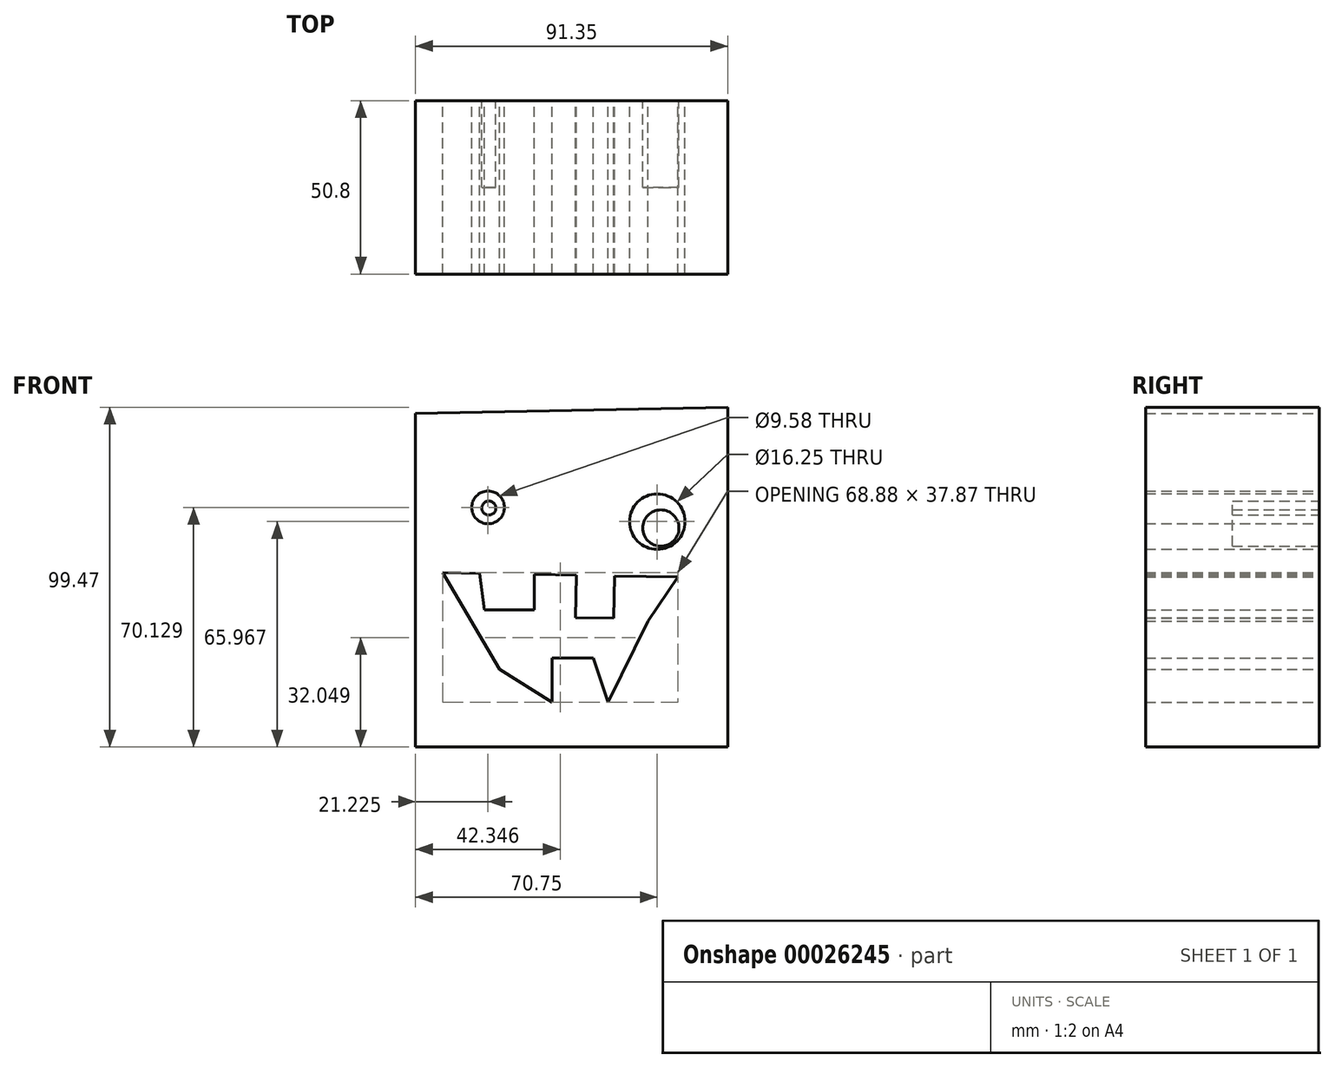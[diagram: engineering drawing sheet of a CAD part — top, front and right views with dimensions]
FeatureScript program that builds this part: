
annotation { "Feature Type Name" : "Feature", "Feature Type Description" : "" }
export const myFeature = defineFeature(function(context is Context, id is Id, definition is map)
    precondition{}
    {
        {
            var Q0;
            Q0=qCreatedBy(makeId("Front.planeOp"),FACE);
            var sketch = newSketch(context, id + "F0", { "sketchPlane" : qUnion([Q0])});
            skLineSegment(sketch, "E0", {"start": v(-46.82, 44.43) * mm, "end": v(-46.82, -53.17) * mm});
            skLineSegment(sketch, "E1", {"start": v(-46.82, -53.17) * mm, "end": v(44.53, -53.17) * mm});
            skLineSegment(sketch, "E2", {"start": v(44.53, -53.17) * mm, "end": v(44.53, 46.3) * mm});
            skLineSegment(sketch, "E3", {"start": v(44.53, 46.3) * mm, "end": v(-46.82, 44.43) * mm});
            skLineSegment(sketch, "E4.bottom", {"start": v(-30.59, 23.83) * mm, "end": v(-15.81, 23.83) * mm});
            skLineSegment(sketch, "E4.top", {"start": v(-30.59, 11.76) * mm, "end": v(-15.81, 11.76) * mm});
            skLineSegment(sketch, "E4.left", {"start": v(-30.59, 23.83) * mm, "end": v(-30.59, 11.76) * mm});
            skLineSegment(sketch, "E4.right", {"start": v(-15.81, 23.83) * mm, "end": v(-15.81, 11.76) * mm});
            skLineSegment(sketch, "E5.bottom", {"start": v(-11.44, 35.69) * mm, "end": v(33.71, 35.69) * mm});
            skLineSegment(sketch, "E5.top", {"start": v(-11.44, 4.47) * mm, "end": v(33.71, 4.47) * mm});
            skLineSegment(sketch, "E5.left", {"start": v(-11.44, 35.69) * mm, "end": v(-11.44, 4.47) * mm});
            skLineSegment(sketch, "E5.right", {"start": v(33.71, 35.69) * mm, "end": v(33.71, 4.47) * mm});
            skLineSegment(sketch, "E6", {"start": v(-38.91, -2.18) * mm, "end": v(-22.27, -30.48) * mm});
            skLineSegment(sketch, "E7", {"start": v(-22.27, -30.48) * mm, "end": v(-6.87, -40.06) * mm});
            skLineSegment(sketch, "E8", {"start": v(-6.87, -40.06) * mm, "end": v(9.57, -40.06) * mm});
            skLineSegment(sketch, "E9", {"start": v(9.57, -40.06) * mm, "end": v(21.23, -16.33) * mm});
            skLineSegment(sketch, "E10", {"start": v(21.23, -16.33) * mm, "end": v(29.96, -3.43) * mm});
            skLineSegment(sketch, "E11", {"start": v(29.96, -3.43) * mm, "end": v(-38.91, -2.18) * mm});
            skLineSegment(sketch, "E12", {"start": v(-28.1, -2.38) * mm, "end": v(-26.64, -13) * mm});
            skLineSegment(sketch, "E13", {"start": v(-26.64, -13) * mm, "end": v(-12.07, -13) * mm});
            skLineSegment(sketch, "E14", {"start": v(-12.07, -13) * mm, "end": v(-12.07, -2.67) * mm});
            skLineSegment(sketch, "E15", {"start": v(-12.07, -2.67) * mm, "end": v(11.44, -3.1) * mm});
            skLineSegment(sketch, "E16", {"start": v(11.44, -3.1) * mm, "end": v(11.21, -15.52) * mm});
            skLineSegment(sketch, "E17", {"start": v(11.21, -15.52) * mm, "end": v(0, -15.31) * mm});
            skLineSegment(sketch, "E18", {"start": v(0, -15.31) * mm, "end": v(0.23, -2.9) * mm});
            skLineSegment(sketch, "E19", {"start": v(-6.87, -40.06) * mm, "end": v(-6.87, -27.16) * mm});
            skLineSegment(sketch, "E20", {"start": v(-6.87, -27.16) * mm, "end": v(5.2, -27.16) * mm});
            skLineSegment(sketch, "E21", {"start": v(5.2, -27.16) * mm, "end": v(9.57, -40.06) * mm});
            skCircle(sketch, "E22", {"center": v(23.93, 12.8) * mm, "radius": 8.13 * mm});
            skCircle(sketch, "E23", {"center": v(-25.6, 16.96) * mm, "radius": 4.8 * mm});
            skSolve(sketch);
        }
        {
            var Q0;
            Q0=makeQuery(id+"F0.imprint","IMPRINT",FACE,{"disambiguationData":[TD([[makeQuery(id+"F0.imprint","IMPRINT",EDGE,{"derivedFrom":sQuery(id+"F0.wireOp",EDGE,"E0")}),1.0]])]});
            var Q1;
            Q1=makeQuery(id+"F0.imprint","IMPRINT",FACE,{"disambiguationData":[TD([[makeQuery(id+"F0.imprint","IMPRINT",EDGE,{"derivedFrom":sQuery(id+"F0.wireOp",EDGE,"E5.bottom")}),-1.0]])]});
            var Q2;
            Q2=makeQuery(id+"F0.imprint","IMPRINT",FACE,{"disambiguationData":[TD([[makeQuery(id+"F0.imprint","IMPRINT",EDGE,{"derivedFrom":sQuery(id+"F0.wireOp",EDGE,"E4.bottom")}),-1.0]])]});
            var Q3;
            {var subQ1=sQuery(id+"F0.wireOp",EDGE,"E12");Q3=makeQuery(id+"F0.imprint","IMPRINT",FACE,{"disambiguationData":[TD([[makeQuery(id+"F0.imprint","IMPRINT",EDGE,{"derivedFrom":subQ1}),1.0]])]});}
            var Q4;
            {var subQ1=sQuery(id+"F0.wireOp",EDGE,"E16");Q4=makeQuery(id+"F0.imprint","IMPRINT",FACE,{"disambiguationData":[TD([[makeQuery(id+"F0.imprint","IMPRINT",EDGE,{"derivedFrom":subQ1}),-1.0]])]});}
            var Q5;
            Q5=makeQuery(id+"F0.imprint","IMPRINT",FACE,{"disambiguationData":[TD([[makeQuery(id+"F0.imprint","IMPRINT",EDGE,{"derivedFrom":sQuery(id+"F0.wireOp",EDGE,"E8")}),1.0]])]});
            extrude(context, id + "F1", {"entities" : qUnion([Q0, Q1, Q2, Q3, Q4, Q5]), "depth" : 50.8 * mm});
        }
        {
            var Q0;
            Q0=qCreatedBy(makeId("Front.planeOp"),FACE);
            var sketch = newSketch(context, id + "F2", { "sketchPlane" : qUnion([Q0])});
            skCircle(sketch, "E24", {"center": v(-25.39, 16.75) * mm, "radius": 2.05 * mm});
            skCircle(sketch, "E25", {"center": v(24.97, 10.92) * mm, "radius": 5.3 * mm});
            skSolve(sketch);
        }
        {
            var Q0;
            Q0=makeQuery(id+"F2.imprint","IMPRINT",FACE,{"disambiguationData":[TD([[makeQuery(id+"F2.imprint","IMPRINT",EDGE,{"derivedFrom":sQuery(id+"F2.wireOp",EDGE,"E24")}),1.0]])]});
            var Q1;
            Q1=makeQuery(id+"F2.imprint","IMPRINT",FACE,{"disambiguationData":[TD([[makeQuery(id+"F2.imprint","IMPRINT",EDGE,{"derivedFrom":sQuery(id+"F2.wireOp",EDGE,"E25")}),1.0]])]});
            extrude(context, id + "F3", {"entities" : qUnion([Q0, Q1]), "depth" : 25.4 * mm});
        }
    });
